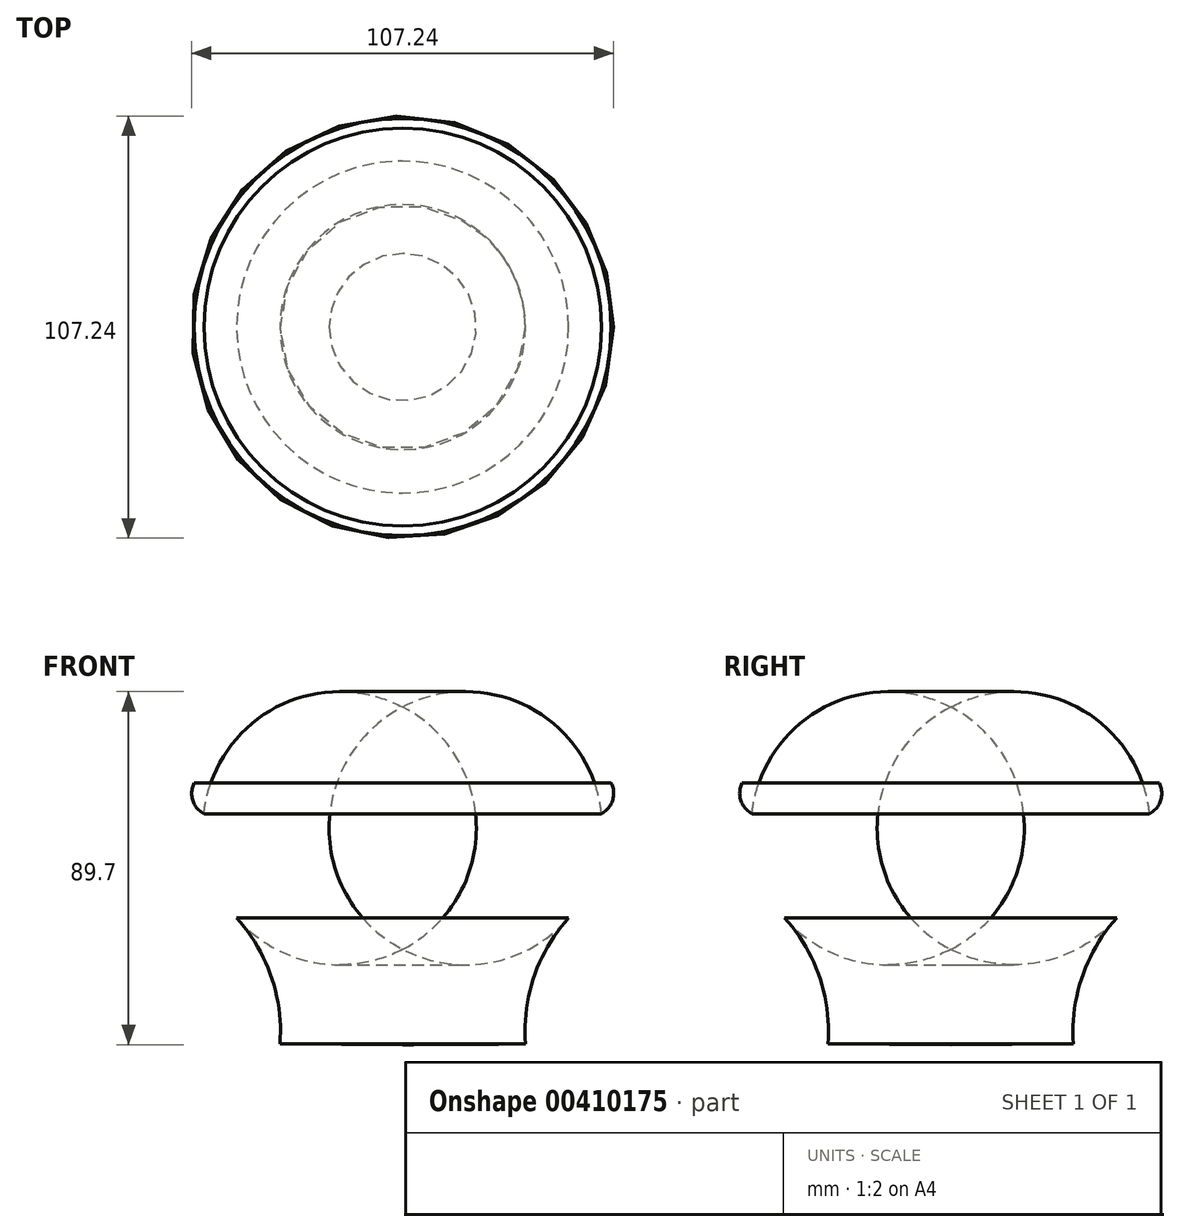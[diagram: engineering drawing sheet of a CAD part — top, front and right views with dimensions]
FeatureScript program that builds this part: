
annotation { "Feature Type Name" : "Feature", "Feature Type Description" : "" }
export const myFeature = defineFeature(function(context is Context, id is Id, definition is map)
    precondition{}
    {
        {
            var Q0;
            Q0=qCreatedBy(makeId("Front.planeOp"),FACE);
            var sketch = newSketch(context, id + "F0", { "sketchPlane" : qUnion([Q0])});
            skArc(sketch, "E0", {"start": v(-50.52, 60.75) * mm, "mid": v(-49.11, 46.66) * mm, "end": v(-42.19, 34.3) * mm});
            skArc(sketch, "E1", {"start": v(-52.98, 68.59) * mm, "mid": v(-53.35, 64.17) * mm, "end": v(-50.52, 60.75) * mm});
            skPoint(sketch, "E2.end.orphan", {"position": v(-48.44, 60.75) * mm});
            skPoint(sketch, "E2.start.orphan", {"position": v(-38.65, 33.57) * mm});
            skPoint(sketch, "E3.end.orphan", {"position": v(-44.46, 33.57) * mm});
            skPoint(sketch, "E3.start.orphan", {"position": v(-33.57, 0) * mm});
            skArc(sketch, "E4.0", {"start": v(-32.88, 0.19) * mm, "mid": v(-34.47, 17.88) * mm, "end": v(-43.3, 33.29) * mm});
            skArc(sketch, "E5.0", {"start": v(-52.1, 59.98) * mm, "mid": v(-50.4, 45.76) * mm, "end": v(-43.32, 33.3) * mm});
            skArc(sketch, "E6.0", {"start": v(-54.32, 69.27) * mm, "mid": v(-54.91, 64.21) * mm, "end": v(-52.1, 59.98) * mm});
            skArc(sketch, "E7", {"start": v(-54.32, 69.27) * mm, "mid": v(-53.31, 69.6) * mm, "end": v(-52.98, 68.59) * mm});
            skLineSegment(sketch, "E8", {"start": v(0, 0) * mm, "end": v(0, 2.08) * mm});
            skLineSegment(sketch, "E9", {"start": v(0, 2.08) * mm, "end": v(-31.17, 2.26) * mm});
            skArc(sketch, "E10.trimOffspring", {"start": v(-31.17, 2.26) * mm, "mid": v(-33.4, 19.4) * mm, "end": v(-42.19, 34.3) * mm});
            skPoint(sketch, "E11.start.orphan", {"position": v(-31.4, 0) * mm});
            skLineSegment(sketch, "E12", {"start": v(-32.88, 0.19) * mm, "end": v(0, 0) * mm});
            skLineSegment(sketch, "E13", {"start": v(-52.98, 68.59) * mm, "end": v(0, 68.59) * mm});
            skLineSegment(sketch, "E14", {"start": v(0, 68.59) * mm, "end": v(0, 0) * mm});
            skSolve(sketch);
        }
        {
            var Q0;
            Q0=makeQuery(id+"F0.imprint","IMPRINT",FACE,{"disambiguationData":[TD([[makeQuery(id+"F0.imprint","IMPRINT",EDGE,{"derivedFrom":sQuery(id+"F0.wireOp",EDGE,"E0")}),1.0]])]});
            var Q1;
            Q1=sQuery(id+"F0.wireOp",EDGE,"E14");
            revolve(context, id + "F1", {"entities" : qUnion([Q0]), "axis" : qUnion([Q1]), "revolveType" : RevolveType.FULL});
        }
    });
